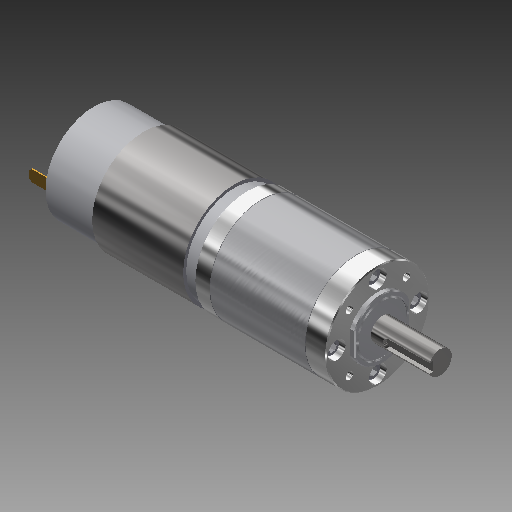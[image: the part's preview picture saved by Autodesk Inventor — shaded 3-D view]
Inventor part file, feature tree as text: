
AUTODESK INVENTOR PART (.ipt)
format: ipt  version: 2018 (Build 220112000, 112)  size: 404,992 bytes
history: native  units: in
note: dims shown in document units (in); Inventor stores cm internally (conversion verified against a paired STEP export)
features: mirror x1, other x1, imported_body x1
ambient origin geometry x8: Origin, YZ Plane, XZ Plane, XY Plane, X Axis, Y Axis, Z Axis, Center Point
bodies: Body1 (feature_tree)
feature tree (3):
  mirror  "Mirror2"
  other  "PG-71"
  imported_body  "Base1"
